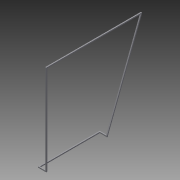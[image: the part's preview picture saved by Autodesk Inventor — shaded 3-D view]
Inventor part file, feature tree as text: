
AUTODESK INVENTOR PART (.ipt)
format: ipt  version: 2013 (Build 170138000, 138)  size: 140,288 bytes
history: native  units: in
note: dims shown in document units (in); Inventor stores cm internally (conversion verified against a paired STEP export)
features: extrude x6, sketch x6
ambient origin geometry x8: Origin, YZ Plane, XZ Plane, XY Plane, X Axis, Y Axis, Z Axis, Center Point
bodies: Solid1 (feature_tree)
feature tree (12):
  extrude  "Extrusion1"  Depth=15.0in
  extrude  "Extrusion2"  Depth=0.25in
  extrude  "Extrusion3"  Depth=1.5in TaperAngle=0.0deg
  extrude  "Extrusion5"  Depth=22.0in
  extrude  "Extrusion6"  Depth=0.25in
  extrude  "Extrusion8"  Depth=14.5in TaperAngle=0.0deg
  sketch  "Sketch1"  dims[d0=0.25in d1=15.0in]
  sketch  "Sketch2"  dims[d2=0.25in d3=0.0in d4=0.25in]
  sketch  "Sketch3"  dims[d5=0.25in d6=1.5in d7=0.0in]
  sketch  "Sketch5"  dims[d8=0.25in d9=22.0in]
  sketch  "Sketch7"  dims[d10=0.25in d11=0.0in d16=0.25in]
  sketch  "Sketch9"  dims[d17=0.25in d18=14.5in d19=0.0in d21=8.5in d22=0.0in d35=21.75in d36=90.0deg d37=8.5in d38=90.0deg d39=0.25in d40=90.0deg d41=0.25in d42=0.25in d43=0.25in d44=0.0in]
